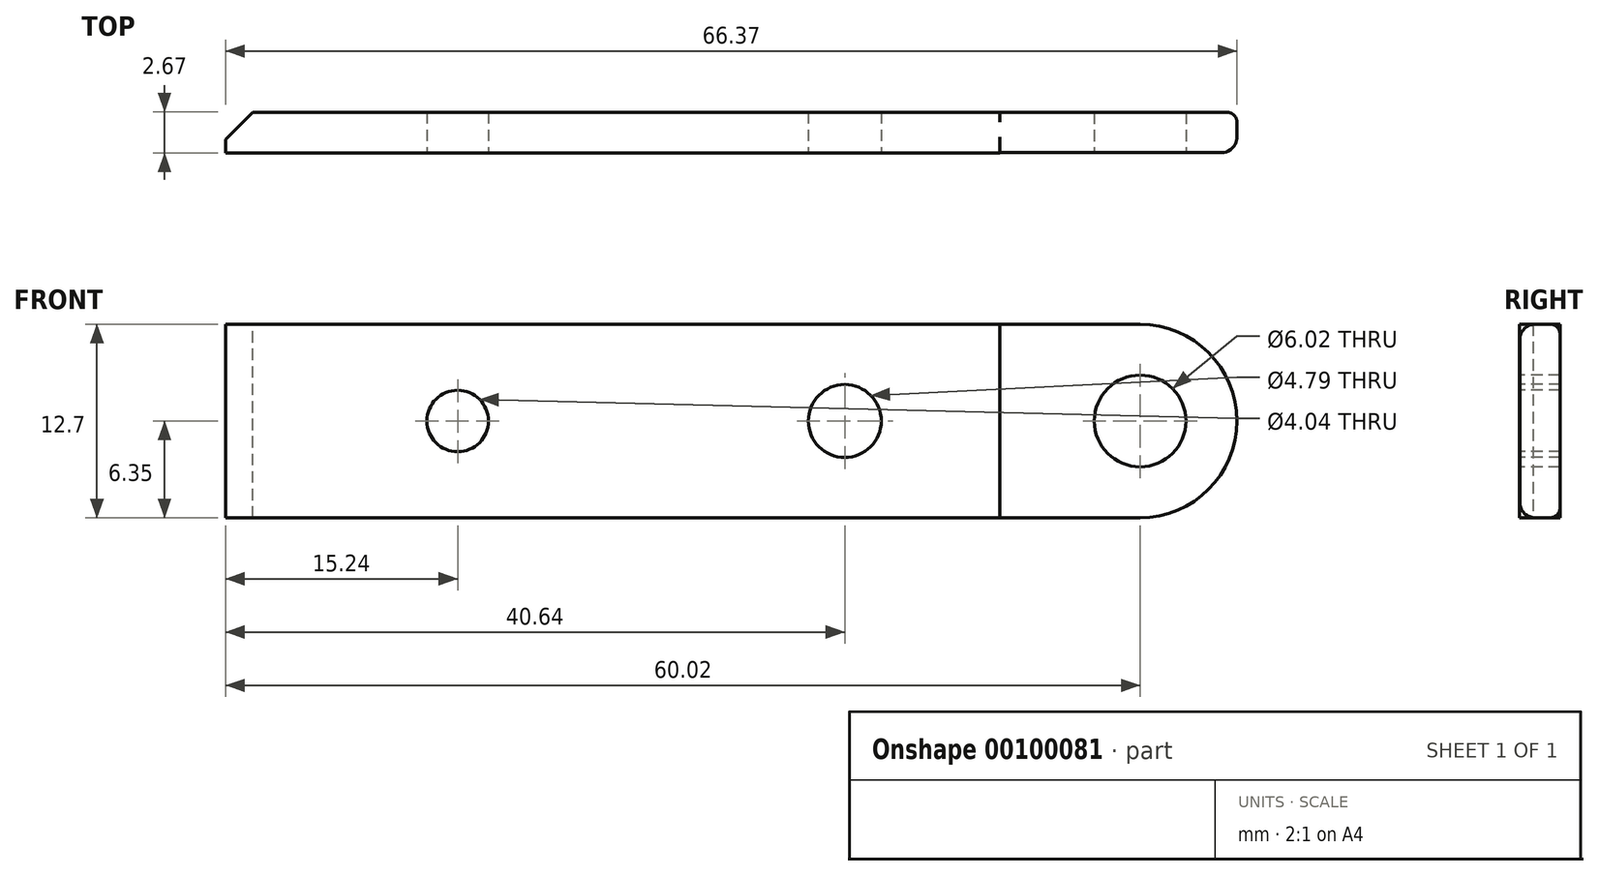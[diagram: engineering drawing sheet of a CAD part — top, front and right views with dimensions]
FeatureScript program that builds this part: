
annotation { "Feature Type Name" : "Feature", "Feature Type Description" : "" }
export const myFeature = defineFeature(function(context is Context, id is Id, definition is map)
    precondition{}
    {
        {
            var Q0;
            Q0=qCreatedBy(makeId("Front.planeOp"),FACE);
            var sketch = newSketch(context, id + "F0", { "sketchPlane" : qUnion([Q0])});
            skLineSegment(sketch, "E0.bottom", {"start": v(0, 0) * mm, "end": v(60.02, 0) * mm});
            skLineSegment(sketch, "E0.top", {"start": v(0, -12.7) * mm, "end": v(60.02, -12.7) * mm});
            skLineSegment(sketch, "E0.left", {"start": v(0, 0) * mm, "end": v(0, -12.7) * mm});
            skLineSegment(sketch, "E0.right", {"start": v(66.37, -6.35) * mm, "end": v(66.37, -6.35) * mm});
            skPoint(sketch, "E1.visualSharp", {"position": v(66.37, -12.7) * mm});
            skArc(sketch, "E1.filletArc", {"start": v(60.02, -12.7) * mm, "mid": v(64.51, -10.84) * mm, "end": v(66.37, -6.35) * mm});
            skPoint(sketch, "E2.visualSharp", {"position": v(66.37, 0) * mm});
            skArc(sketch, "E2.filletArc", {"start": v(66.37, -6.35) * mm, "mid": v(64.51, -1.86) * mm, "end": v(60.02, 0) * mm});
            skSolve(sketch);
        }
        {
            var Q0;
            Q0 = qSketchRegion(id + "F0", true);
            extrude(context, id + "F1", {"entities" : qUnion([Q0]), "oppositeDirection" : true, "depth" : 2.67 * mm});
        }
        {
            var Q0;
            Q0=makeQuery(id+"F1.opExtrude","CAP_FACE",FACE,{"disambiguationData":[OSD([sQuery(id+"F0.wireOp",EDGE,"E0.bottom"),sQuery(id+"F0.wireOp",EDGE,"E0.top"),sQuery(id+"F0.wireOp",EDGE,"E0.left"),sQuery(id+"F0.wireOp",EDGE,"E1.filletArc"),sQuery(id+"F0.wireOp",EDGE,"E2.filletArc")])],"isStart":true});
            var sketch = newSketch(context, id + "F2", { "sketchPlane" : qUnion([Q0])});
            skPoint(sketch, "E3", {"position": v(60.02, -6.35) * mm});
            skPoint(sketch, "E4", {"position": v(15.24, -6.35) * mm});
            skPoint(sketch, "E5", {"position": v(40.64, -6.35) * mm});
            skSolve(sketch);
        }
        {
            var Q0;
            Q0=sQuery(id+"F2.wireOp",VERTEX,"E3");
            var Q1;
            Q1=makeQuery(id+"F1.opExtrude","SWEPT_BODY",BODY,{"disambiguationData":[OSD([sQuery(id+"F0.wireOp",EDGE,"E0.bottom"),sQuery(id+"F0.wireOp",EDGE,"E0.top"),sQuery(id+"F0.wireOp",EDGE,"E0.left"),sQuery(id+"F0.wireOp",EDGE,"E1.filletArc"),sQuery(id+"F0.wireOp",EDGE,"E2.filletArc")])]});
            hole(context, id + "F3", {"style" : HoleStyle.SIMPLE, "endStyle" : HoleEndStyle.THROUGH, "holeDiameter" : 6.02 * mm, "startFromSketch" : true, "locations" : qUnion([Q0]), "scope" : qUnion([Q1]), "isTappedThrough" : true});
        }
        {
            var Q0;
            Q0=sQuery(id+"F2.wireOp",VERTEX,"E5");
            var Q1;
            Q1=makeQuery(id+"F1.opExtrude","SWEPT_BODY",BODY,{"disambiguationData":[OSD([sQuery(id+"F0.wireOp",EDGE,"E0.bottom"),sQuery(id+"F0.wireOp",EDGE,"E0.top"),sQuery(id+"F0.wireOp",EDGE,"E0.left"),sQuery(id+"F0.wireOp",EDGE,"E1.filletArc"),sQuery(id+"F0.wireOp",EDGE,"E2.filletArc")])]});
            hole(context, id + "F4", {"style" : HoleStyle.SIMPLE, "endStyle" : HoleEndStyle.THROUGH, "holeDiameter" : 4.8 * mm, "startFromSketch" : true, "locations" : qUnion([Q0]), "scope" : qUnion([Q1]), "isTappedThrough" : true});
        }
        {
            var Q0;
            Q0=sQuery(id+"F2.wireOp",VERTEX,"E4");
            var Q1;
            Q1=makeQuery(id+"F1.opExtrude","SWEPT_BODY",BODY,{"disambiguationData":[OSD([sQuery(id+"F0.wireOp",EDGE,"E0.bottom"),sQuery(id+"F0.wireOp",EDGE,"E0.top"),sQuery(id+"F0.wireOp",EDGE,"E0.left"),sQuery(id+"F0.wireOp",EDGE,"E1.filletArc"),sQuery(id+"F0.wireOp",EDGE,"E2.filletArc")])]});
            hole(context, id + "F5", {"style" : HoleStyle.SIMPLE, "endStyle" : HoleEndStyle.THROUGH, "standardTappedOrClearance" : lookupTablePath({ "standard" : "ANSI", "engagement" : "75%", "pitch" : "32 tpi", "size" : "#10", "type" : "Tapped" }), "standardBlindInLast" : lookupTablePath({ "standard" : "ANSI", "engagement" : "75%", "pitch" : "32 tpi", "size" : "#10", "type" : "Tapped" }), "holeDiameter" : 4.04 * mm, "startFromSketch" : true, "locations" : qUnion([Q0]), "scope" : qUnion([Q1]), "isTappedThrough" : true, "majorDiameter" : 4.83 * mm, "showTappedDepth" : true});
        }
        {
            var Q0;
            Q0=makeQuery(id+"F1.opExtrude","CAP_FACE",FACE,{"disambiguationData":[OSD([sQuery(id+"F0.wireOp",EDGE,"E0.bottom"),sQuery(id+"F0.wireOp",EDGE,"E0.top"),sQuery(id+"F0.wireOp",EDGE,"E0.left"),sQuery(id+"F0.wireOp",EDGE,"E1.filletArc"),sQuery(id+"F0.wireOp",EDGE,"E2.filletArc")])],"isStart":true});
            var sketch = newSketch(context, id + "F6", { "sketchPlane" : qUnion([Q0])});
            skLineSegment(sketch, "E6.bottom", {"start": v(50.8, 11.26) * mm, "end": v(83.68, 11.26) * mm});
            skLineSegment(sketch, "E6.top", {"start": v(50.8, -31.18) * mm, "end": v(83.68, -31.18) * mm});
            skLineSegment(sketch, "E6.left", {"start": v(50.8, 11.26) * mm, "end": v(50.8, -31.18) * mm});
            skLineSegment(sketch, "E6.right", {"start": v(83.68, 11.26) * mm, "end": v(83.68, -31.18) * mm});
            skSolve(sketch);
        }
        {
            var Q0;
            Q0 = qSketchRegion(id + "F6", true);
            extrude(context, id + "F7", {"entities" : qUnion([Q0]), "operationType" : NewBodyOperationType.REMOVE, "oppositeDirection" : true, "depth" : 0.01 * mm});
        }
        {
            var Q0;
            Q0=makeQuery(id+"F1.opExtrude","CAP_FACE",FACE,{"disambiguationData":[OSD([sQuery(id+"F0.wireOp",EDGE,"E0.bottom"),sQuery(id+"F0.wireOp",EDGE,"E0.top"),sQuery(id+"F0.wireOp",EDGE,"E0.left"),sQuery(id+"F0.wireOp",EDGE,"E1.filletArc"),sQuery(id+"F0.wireOp",EDGE,"E2.filletArc")])],"isStart":false});
            var sketch = newSketch(context, id + "F8", { "sketchPlane" : qUnion([Q0])});
            skLineSegment(sketch, "E7.bottom", {"start": v(-50.8, -16.89) * mm, "end": v(-78.59, -16.89) * mm});
            skLineSegment(sketch, "E7.top", {"start": v(-50.8, 8.68) * mm, "end": v(-78.59, 8.68) * mm});
            skLineSegment(sketch, "E7.left", {"start": v(-50.8, -16.89) * mm, "end": v(-50.8, 8.68) * mm});
            skLineSegment(sketch, "E7.right", {"start": v(-78.59, -16.89) * mm, "end": v(-78.59, 8.68) * mm});
            skSolve(sketch);
        }
        {
            var Q0;
            Q0 = qSketchRegion(id + "F8", true);
            extrude(context, id + "F9", {"entities" : qUnion([Q0]), "operationType" : NewBodyOperationType.REMOVE, "oppositeDirection" : true, "depth" : 0.01 * mm});
        }
        {
            var Q0;
            Q0=makeQuery(id+"F7.boolean.opBoolean","INTERSECT",EDGE,{"derivedFrom":[makeQuery(id+"F1.opExtrude","SWEPT_FACE",FACE,{"disambiguationData":[OSD([sQuery(id+"F0.wireOp",EDGE,"E0.top")])]}),makeQuery(id+"F7.opExtrude","CAP_FACE",FACE,{"disambiguationData":[OSD([sQuery(id+"F6.wireOp",EDGE,"E6.bottom"),sQuery(id+"F6.wireOp",EDGE,"E6.top"),sQuery(id+"F6.wireOp",EDGE,"E6.left"),sQuery(id+"F6.wireOp",EDGE,"E6.right")])],"isStart":false})]});
            fillet(context, id + "F10", {"entities" : qUnion([Q0]), "radius" : 1.02 * mm, "tangentPropagation" : true, "allowEdgeOverflow" : false});
        }
        {
            var Q0;
            Q0=makeQuery(id+"F9.boolean.opBoolean","INTERSECT",EDGE,{"derivedFrom":[makeQuery(id+"F1.opExtrude","SWEPT_FACE",FACE,{"disambiguationData":[OSD([sQuery(id+"F0.wireOp",EDGE,"E0.bottom")])]}),makeQuery(id+"F9.opExtrude","CAP_FACE",FACE,{"disambiguationData":[OSD([sQuery(id+"F8.wireOp",EDGE,"E7.bottom"),sQuery(id+"F8.wireOp",EDGE,"E7.top"),sQuery(id+"F8.wireOp",EDGE,"E7.left"),sQuery(id+"F8.wireOp",EDGE,"E7.right")])],"isStart":false})]});
            fillet(context, id + "F11", {"entities" : qUnion([Q0]), "radius" : 0.64 * mm, "tangentPropagation" : true, "allowEdgeOverflow" : false});
        }
        {
            var Q0;
            Q0=makeQuery(id+"F1.opExtrude","CAP_EDGE",EDGE,{"disambiguationData":[OSD([sQuery(id+"F0.wireOp",EDGE,"E0.left")])],"isStart":false});
            chamfer(context, id + "F12", {"entities" : qUnion([Q0]), "chamferType" : ChamferType.OFFSET_ANGLE, "width" : 1.78 * mm, "oppositeDirection" : false, "angle" : 45 * degree, "tangentPropagation" : true});
        }
    });
